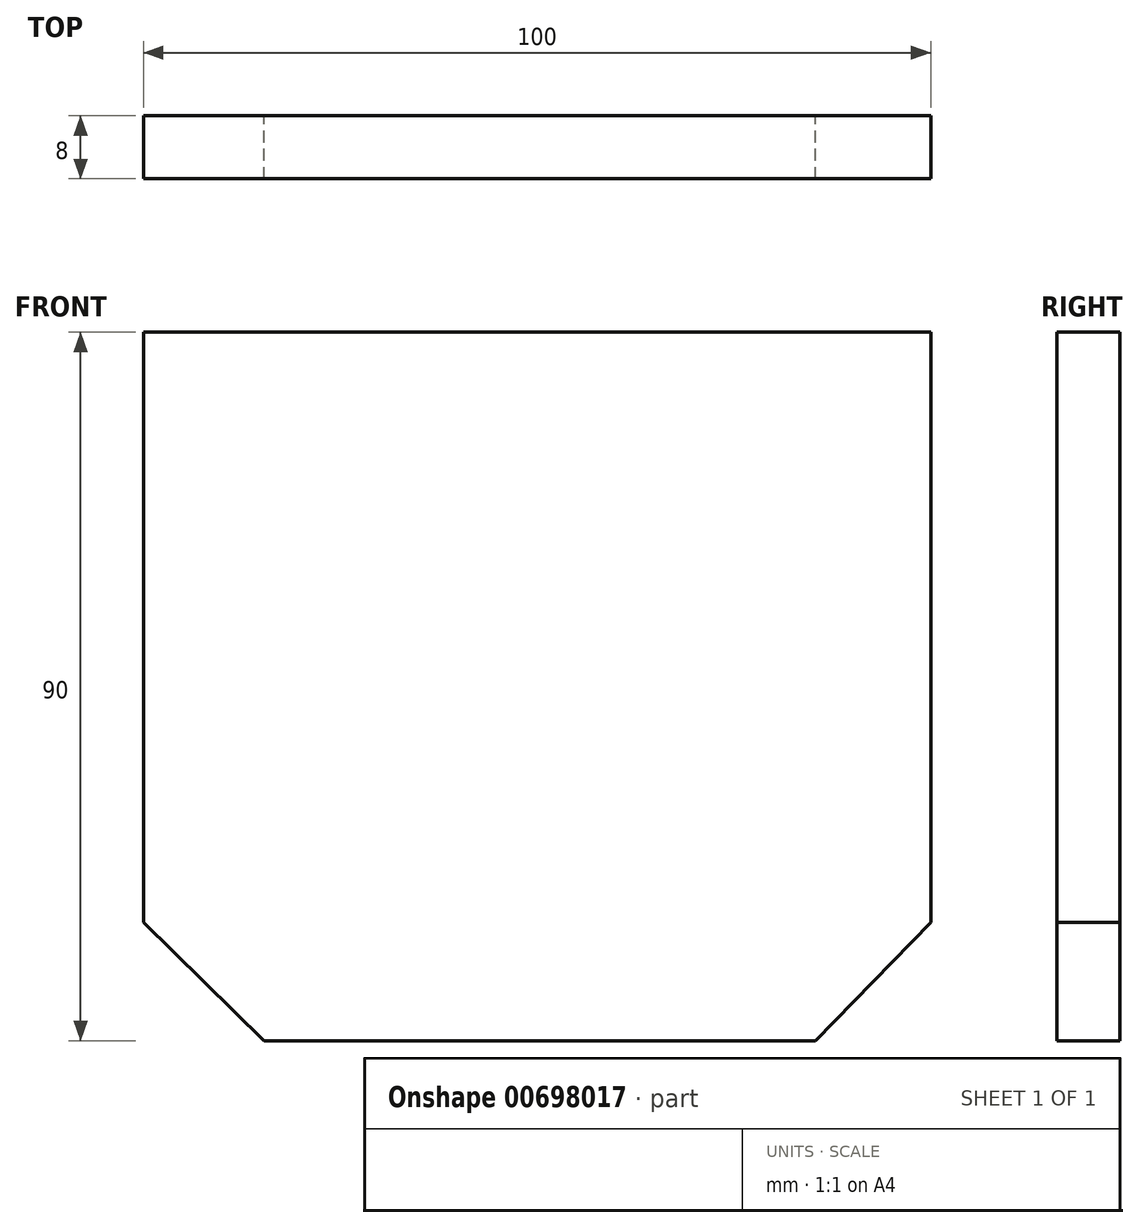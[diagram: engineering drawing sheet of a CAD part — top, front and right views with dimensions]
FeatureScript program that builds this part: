
annotation { "Feature Type Name" : "Feature", "Feature Type Description" : "" }
export const myFeature = defineFeature(function(context is Context, id is Id, definition is map)
    precondition{}
    {
        {
            var Q0;
            Q0=qCreatedBy(makeId("Front.planeOp"),FACE);
            var sketch = newSketch(context, id + "F0", { "sketchPlane" : qUnion([Q0])});
            skLineSegment(sketch, "E0", {"start": v(0, 0) * mm, "end": v(0, 75) * mm});
            skLineSegment(sketch, "E1", {"start": v(0, 75) * mm, "end": v(100, 75) * mm});
            skLineSegment(sketch, "E2", {"start": v(100, 75) * mm, "end": v(100, 0) * mm});
            skLineSegment(sketch, "E3", {"start": v(100, 0) * mm, "end": v(85.33, -15) * mm});
            skLineSegment(sketch, "E4", {"start": v(85.33, -15) * mm, "end": v(15.33, -15) * mm});
            skLineSegment(sketch, "E5", {"start": v(15.33, -15) * mm, "end": v(0, 0) * mm});
            skSolve(sketch);
        }
        {
            var Q0;
            Q0=makeQuery(id+"F0.imprint","IMPRINT",FACE,{"disambiguationData":[TD([[makeQuery(id+"F0.imprint","IMPRINT",EDGE,{"derivedFrom":sQuery(id+"F0.wireOp",EDGE,"E0")}),-1.0]])]});
            extrude(context, id + "F1", {"entities" : qUnion([Q0]), "depth" : 8 * mm, "offsetDistance" : 25 * mm});
        }
    });
